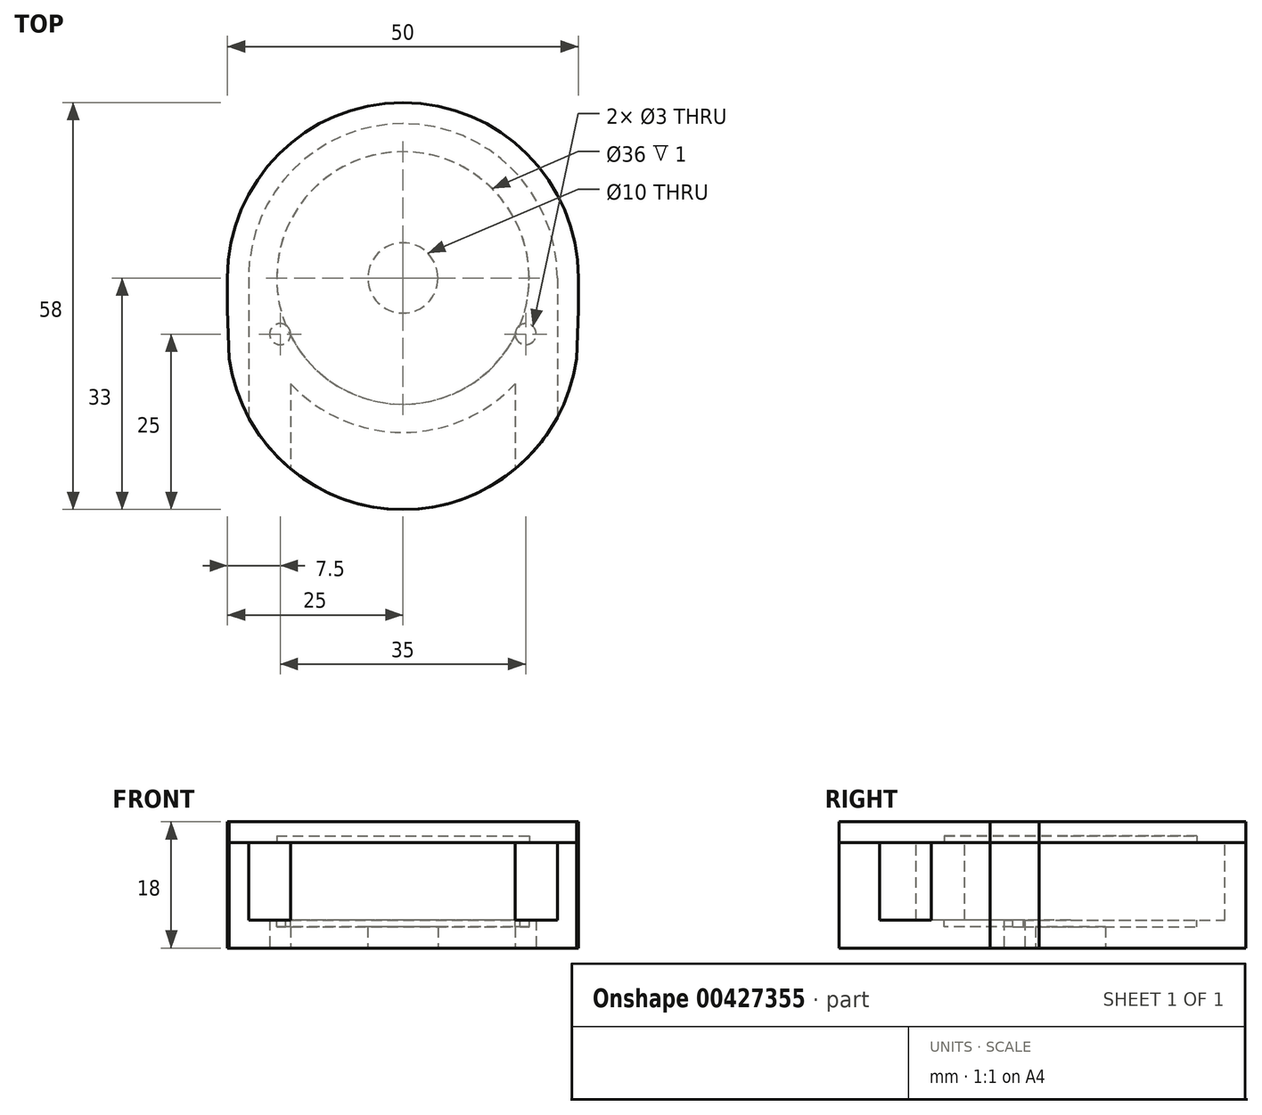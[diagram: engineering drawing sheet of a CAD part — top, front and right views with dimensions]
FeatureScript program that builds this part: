
annotation { "Feature Type Name" : "Feature", "Feature Type Description" : "" }
export const myFeature = defineFeature(function(context is Context, id is Id, definition is map)
    precondition{}
    {
        {
            var Q0;
            Q0=qCreatedBy(makeId("Top.planeOp"),FACE);
            var sketch = newSketch(context, id + "F0", { "sketchPlane" : qUnion([Q0])});
            skArc(sketch, "E0", {"start": v(-24.75, -3.5) * mm, "mid": v(0, -25) * mm, "end": v(24.75, -3.5) * mm});
            skLineSegment(sketch, "E1.rect.bottom", {"start": v(25, 3.5) * mm, "end": v(17.5, 3.5) * mm, "construction": true});
            skLineSegment(sketch, "E1.rect.top", {"start": v(17.5, -3.5) * mm, "end": v(-17.5, -3.5) * mm, "construction": true});
            skLineSegment(sketch, "E1.rect.left", {"start": v(17.5, 3.5) * mm, "end": v(17.5, -3.5) * mm, "construction": true});
            skArc(sketch, "E2", {"start": v(-17.5, 3.5) * mm, "mid": v(-21, 0) * mm, "end": v(-17.5, -3.5) * mm, "construction": true});
            skArc(sketch, "E3", {"start": v(17.5, -3.5) * mm, "mid": v(21, 0) * mm, "end": v(17.5, 3.5) * mm, "construction": true});
            skCircle(sketch, "E4", {"center": v(0, 8) * mm, "radius": 5 * mm});
            skArc(sketch, "E5", {"start": v(25, 8) * mm, "mid": v(0, 33) * mm, "end": v(-25, 8) * mm});
            skLineSegment(sketch, "E6", {"start": v(-25, 8) * mm, "end": v(-25, 3.5) * mm});
            skLineSegment(sketch, "E7", {"start": v(25, 8) * mm, "end": v(25, 3.5) * mm});
            skPoint(sketch, "E8.orphan", {"position": v(-25, 0) * mm});
            skLineSegment(sketch, "E9.trimOffspring", {"start": v(-17.5, 3.5) * mm, "end": v(-25, 3.5) * mm, "construction": true});
            skPoint(sketch, "E10.orphan", {"position": v(25, 0) * mm});
            skCircle(sketch, "E11", {"center": v(-17.5, 0) * mm, "radius": 1.5 * mm});
            skCircle(sketch, "E12", {"center": v(17.5, 0) * mm, "radius": 1.5 * mm});
            skLineSegment(sketch, "E13", {"start": v(-25, 3.5) * mm, "end": v(-24.75, -3.5) * mm});
            skLineSegment(sketch, "E14", {"start": v(25, 3.5) * mm, "end": v(24.75, -3.5) * mm});
            skSolve(sketch);
        }
        {
            var Q0;
            Q0=qSketchRegion(id+"F0",true);
            extrude(context, id + "F1", {"entities" : qUnion([Q0]), "depth" : 15 * mm});
        }
        {
            var Q0;
            Q0=makeQuery(id+"F1.opExtrude","CAP_FACE",FACE,{"disambiguationData":[OSD([sQuery(id+"F0.wireOp",EDGE,"E0"),sQuery(id+"F0.wireOp",EDGE,"E1.rect.bottom"),sQuery(id+"F0.wireOp",EDGE,"E1.rect.top"),sQuery(id+"F0.wireOp",EDGE,"E2"),sQuery(id+"F0.wireOp",EDGE,"E3"),sQuery(id+"F0.wireOp",EDGE,"E4"),sQuery(id+"F0.wireOp",EDGE,"E5"),sQuery(id+"F0.wireOp",EDGE,"E6"),sQuery(id+"F0.wireOp",EDGE,"E7"),sQuery(id+"F0.wireOp",EDGE,"E9.trimOffspring"),sQuery(id+"F0.wireOp",EDGE,"E11"),sQuery(id+"F0.wireOp",EDGE,"E12")])],"isStart":false});
            var sketch = newSketch(context, id + "F2", { "sketchPlane" : qUnion([Q0])});
            skArc(sketch, "E15", {"start": v(-16, -7.1) * mm, "mid": v(0, -14) * mm, "end": v(16, -7.1) * mm});
            skLineSegment(sketch, "E16.bottom", {"start": v(-22, 8) * mm, "end": v(-16, 8) * mm});
            skLineSegment(sketch, "E16.top", {"start": v(-22, -19.2) * mm, "end": v(-16, -19.2) * mm});
            skLineSegment(sketch, "E16.left", {"start": v(-22, 8) * mm, "end": v(-22, -19.2) * mm});
            skLineSegment(sketch, "E16.right", {"start": v(-16, 8) * mm, "end": v(-16, -19.2) * mm});
            skLineSegment(sketch, "E17.bottom", {"start": v(22, 8) * mm, "end": v(16, 8) * mm});
            skLineSegment(sketch, "E17.top", {"start": v(22, -19.2) * mm, "end": v(16, -19.2) * mm});
            skLineSegment(sketch, "E17.left", {"start": v(22, 8) * mm, "end": v(22, -19.2) * mm});
            skLineSegment(sketch, "E17.right", {"start": v(16, 8) * mm, "end": v(16, -19.2) * mm});
            skArc(sketch, "E18.trimOffspring", {"start": v(22, 8) * mm, "mid": v(0, 30) * mm, "end": v(-22, 8) * mm});
            skSolve(sketch);
        }
        {
            var Q0;
            Q0=qSketchRegion(id+"F2",true);
            extrude(context, id + "F3", {"entities" : qUnion([Q0]), "operationType" : NewBodyOperationType.REMOVE, "oppositeDirection" : true, "depth" : 11 * mm});
        }
        {
            var Q0;
            {var subQ0=sQuery(id+"F0.wireOp",EDGE,"E0");Q0=makeQuery(id+"F3.boolean.opBoolean","SPLIT",FACE,{"disambiguationData":[TD([makeQuery(id+"F3.opExtrude","SWEPT_FACE",FACE,{"disambiguationData":[OSD([sQuery(id+"F2.wireOp",EDGE,"E15")])]})])],"derivedFrom":makeQuery(id+"F1.opExtrude","CAP_FACE",FACE,{"disambiguationData":[OSD([subQ0,sQuery(id+"F0.wireOp",EDGE,"E4"),sQuery(id+"F0.wireOp",EDGE,"E5"),sQuery(id+"F0.wireOp",EDGE,"E6"),sQuery(id+"F0.wireOp",EDGE,"E7"),sQuery(id+"F0.wireOp",EDGE,"E11"),sQuery(id+"F0.wireOp",EDGE,"E12"),sQuery(id+"F0.wireOp",EDGE,"E13"),sQuery(id+"F0.wireOp",EDGE,"E14")])],"isStart":false})});}
            var sketch = newSketch(context, id + "F4", { "sketchPlane" : qUnion([Q0])});
            skArc(sketch, "E19.3", {"start": v(-24.75, -3.5) * mm, "mid": v(-23.75, -7.8) * mm, "end": v(-22, -11.87) * mm});
            skArc(sketch, "E20.0", {"start": v(-22, -11.87) * mm, "mid": v(-19.35, -15.83) * mm, "end": v(-16, -19.2) * mm});
            skArc(sketch, "E21.0", {"start": v(-16, -19.2) * mm, "mid": v(0, -25) * mm, "end": v(16, -19.2) * mm});
            skArc(sketch, "E21.1", {"start": v(16, -19.2) * mm, "mid": v(19.35, -15.83) * mm, "end": v(22, -11.87) * mm});
            skArc(sketch, "E21.2", {"start": v(22, -11.87) * mm, "mid": v(23.75, -7.8) * mm, "end": v(24.75, -3.5) * mm});
            skLineSegment(sketch, "E21.3", {"start": v(25, 3.5) * mm, "end": v(24.75, -3.5) * mm});
            skLineSegment(sketch, "E21.4", {"start": v(25, 8) * mm, "end": v(25, 3.5) * mm});
            skArc(sketch, "E21.5", {"start": v(25, 8) * mm, "mid": v(0, 33) * mm, "end": v(-25, 8) * mm});
            skLineSegment(sketch, "E21.6", {"start": v(-25, 8) * mm, "end": v(-25, 3.5) * mm});
            skLineSegment(sketch, "E21.7", {"start": v(-25, 3.5) * mm, "end": v(-24.75, -3.5) * mm});
            skSolve(sketch);
        }
        {
            var Q0;
            Q0=qSketchRegion(id+"F4",true);
            extrude(context, id + "F5", {"entities" : qUnion([Q0]), "depth" : 3 * mm});
        }
        {
            var Q0;
            Q0=makeQuery(id+"F3.boolean.opBoolean","COPY",FACE,{"derivedFrom":makeQuery(id+"F3.opExtrude","CAP_FACE",FACE,{"disambiguationData":[OSD([sQuery(id+"F2.wireOp",EDGE,"E15"),sQuery(id+"F2.wireOp",EDGE,"E16.top"),sQuery(id+"F2.wireOp",EDGE,"E16.left"),sQuery(id+"F2.wireOp",EDGE,"E16.right"),sQuery(id+"F2.wireOp",EDGE,"E17.top"),sQuery(id+"F2.wireOp",EDGE,"E17.left"),sQuery(id+"F2.wireOp",EDGE,"E17.right"),sQuery(id+"F2.wireOp",EDGE,"E18.trimOffspring")])],"isStart":false})});
            var sketch = newSketch(context, id + "F6", { "sketchPlane" : qUnion([Q0])});
            skCircle(sketch, "E22", {"center": v(0, 8) * mm, "radius": 18 * mm});
            skSolve(sketch);
        }
        {
            var Q0;
            Q0=qSketchRegion(id+"F6",true);
            extrude(context, id + "F7", {"entities" : qUnion([Q0]), "operationType" : NewBodyOperationType.REMOVE, "oppositeDirection" : true, "depth" : 1 * mm});
        }
        {
            var Q0;
            Q0=makeQuery(id+"F5.opExtrude","CAP_FACE",FACE,{"disambiguationData":[OSD([sQuery(id+"F4.wireOp",EDGE,"E19.3"),sQuery(id+"F4.wireOp",EDGE,"E20.0"),sQuery(id+"F4.wireOp",EDGE,"E21.0"),sQuery(id+"F4.wireOp",EDGE,"E21.1"),sQuery(id+"F4.wireOp",EDGE,"E21.2"),sQuery(id+"F4.wireOp",EDGE,"E21.3"),sQuery(id+"F4.wireOp",EDGE,"E21.4"),sQuery(id+"F4.wireOp",EDGE,"E21.5"),sQuery(id+"F4.wireOp",EDGE,"E21.6"),sQuery(id+"F4.wireOp",EDGE,"E21.7")])],"isStart":true});
            var sketch = newSketch(context, id + "F8", { "sketchPlane" : qUnion([Q0])});
            skCircle(sketch, "E23.0", {"center": v(0, -8) * mm, "radius": 18 * mm});
            skSolve(sketch);
        }
        {
            var Q0;
            Q0=qSketchRegion(id+"F8",true);
            extrude(context, id + "F9", {"entities" : qUnion([Q0]), "operationType" : NewBodyOperationType.REMOVE, "oppositeDirection" : true, "depth" : 1 * mm});
        }
    });
